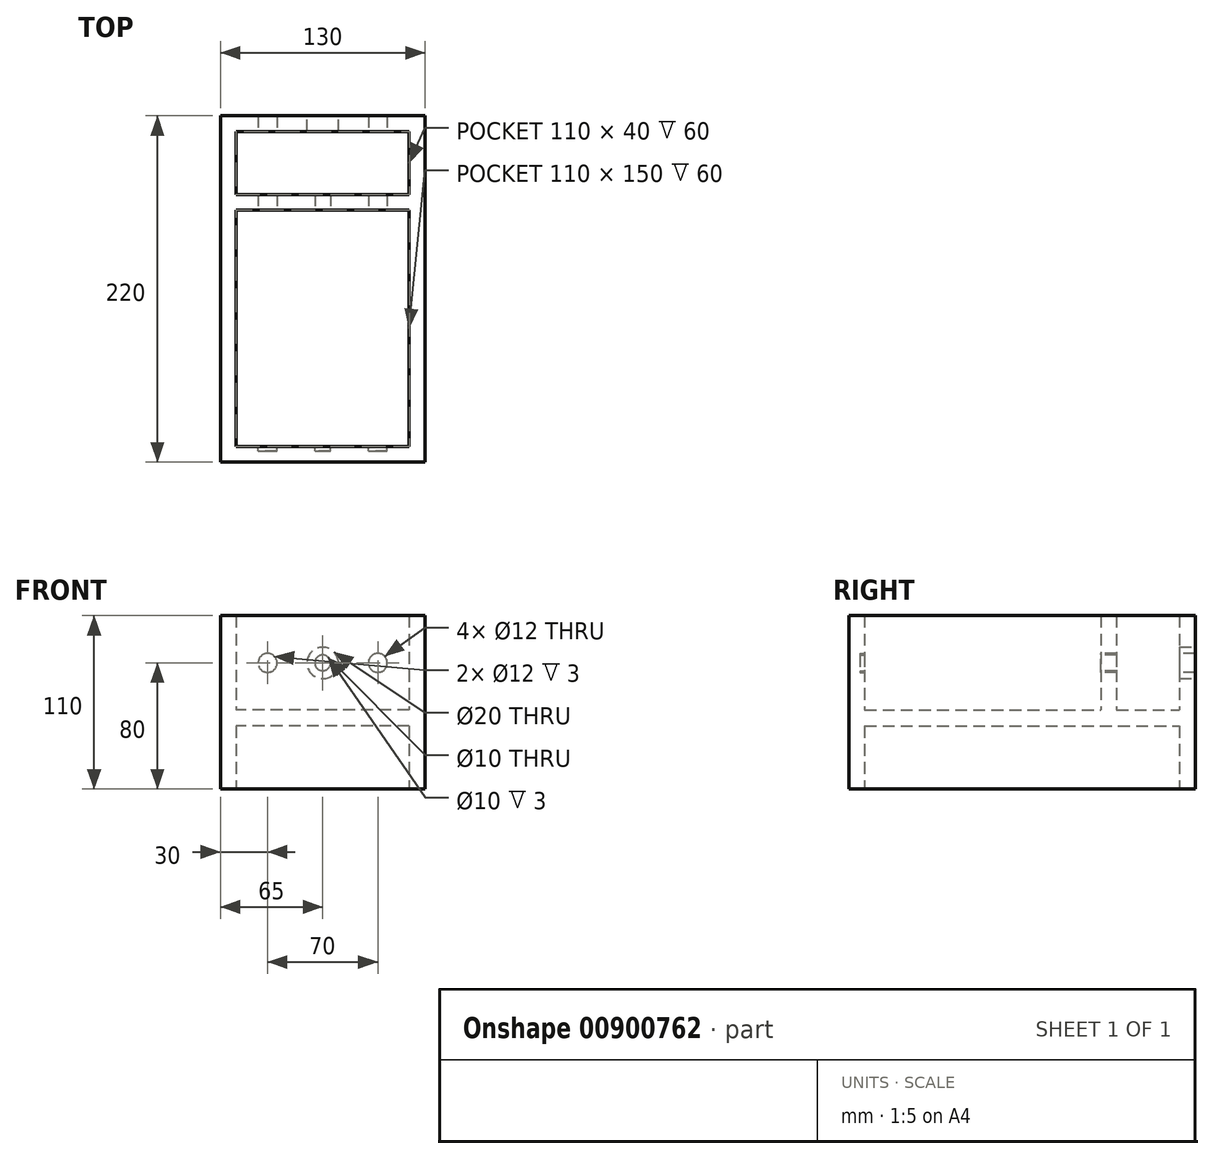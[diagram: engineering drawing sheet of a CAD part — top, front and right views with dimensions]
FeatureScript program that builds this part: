
annotation { "Feature Type Name" : "Feature", "Feature Type Description" : "" }
export const myFeature = defineFeature(function(context is Context, id is Id, definition is map)
    precondition{}
    {
        {
            var Q0;
            Q0=qCreatedBy(makeId("Right.planeOp"),FACE);
            var sketch = newSketch(context, id + "F0", { "sketchPlane" : qUnion([Q0])});
            skLineSegment(sketch, "E0.bottom", {"start": v(-110, 70) * mm, "end": v(-100, 70) * mm});
            skLineSegment(sketch, "E0.top", {"start": v(-110, -40) * mm, "end": v(-100, -40) * mm});
            skLineSegment(sketch, "E0.left", {"start": v(-110, 70) * mm, "end": v(-110, -40) * mm});
            skLineSegment(sketch, "E0.right", {"start": v(-100, 70) * mm, "end": v(-100, -40) * mm});
            skLineSegment(sketch, "E1.bottom", {"start": v(-100, 0) * mm, "end": v(100, 0) * mm});
            skLineSegment(sketch, "E1.top", {"start": v(-100, 10) * mm, "end": v(100, 10) * mm});
            skLineSegment(sketch, "E1.left", {"start": v(-100, 10) * mm, "end": v(-100, 0) * mm});
            skLineSegment(sketch, "E1.right", {"start": v(100, 10) * mm, "end": v(100, 0) * mm});
            skLineSegment(sketch, "E2.bottom", {"start": v(50, 70) * mm, "end": v(60, 70) * mm});
            skLineSegment(sketch, "E2.top", {"start": v(50, 10) * mm, "end": v(60, 10) * mm});
            skLineSegment(sketch, "E2.left", {"start": v(50, 70) * mm, "end": v(50, 10) * mm});
            skLineSegment(sketch, "E2.right", {"start": v(60, 70) * mm, "end": v(60, 10) * mm});
            skLineSegment(sketch, "E3.bottom", {"start": v(110, 70) * mm, "end": v(100, 70) * mm});
            skLineSegment(sketch, "E3.top", {"start": v(110, -40) * mm, "end": v(100, -40) * mm});
            skLineSegment(sketch, "E3.left", {"start": v(110, 70) * mm, "end": v(110, -40) * mm});
            skLineSegment(sketch, "E3.right", {"start": v(100, 70) * mm, "end": v(100, -40) * mm});
            skSolve(sketch);
        }
        {
            var Q0;
            {var subQ2=sQuery(id+"F0.wireOp",EDGE,"E3.bottom");Q0=makeQuery(id+"F0.imprint","IMPRINT",FACE,{"disambiguationData":[TD([[makeQuery(id+"F0.imprint","IMPRINT",EDGE,{"derivedFrom":subQ2}),1.0]])]});}
            var Q1;
            {var subQ5=sQuery(id+"F0.wireOp",EDGE,"E1.bottom");Q1=makeQuery(id+"F0.imprint","IMPRINT",FACE,{"disambiguationData":[TD([[makeQuery(id+"F0.imprint","IMPRINT",EDGE,{"derivedFrom":subQ5}),1.0]])]});}
            var Q2;
            Q2=makeQuery(id+"F0.imprint","IMPRINT",FACE,{"disambiguationData":[TD([[makeQuery(id+"F0.imprint","IMPRINT",EDGE,{"derivedFrom":sQuery(id+"F0.wireOp",EDGE,"E2.bottom")}),-1.0]])]});
            var Q3;
            {var subQ1=sQuery(id+"F0.wireOp",EDGE,"E0.bottom");Q3=makeQuery(id+"F0.imprint","IMPRINT",FACE,{"disambiguationData":[TD([[makeQuery(id+"F0.imprint","IMPRINT",EDGE,{"derivedFrom":subQ1}),-1.0]])]});}
            extrude(context, id + "F1", {"entities" : qUnion([Q0, Q1, Q2, Q3]), "endBound" : BoundingType.SYMMETRIC, "depth" : 110 * mm, "offsetDistance" : 25 * mm});
        }
        {
            var Q0;
            Q0=makeQuery(id+"F1.opExtrude","CAP_FACE",FACE,{"disambiguationData":[OSD([sQuery(id+"F0.wireOp",EDGE,"E0.bottom"),sQuery(id+"F0.wireOp",EDGE,"E0.top"),sQuery(id+"F0.wireOp",EDGE,"E0.left"),sQuery(id+"F0.wireOp",EDGE,"E0.right"),sQuery(id+"F0.wireOp",EDGE,"E1.bottom"),sQuery(id+"F0.wireOp",EDGE,"E1.top"),sQuery(id+"F0.wireOp",EDGE,"E2.bottom"),sQuery(id+"F0.wireOp",EDGE,"E2.left"),sQuery(id+"F0.wireOp",EDGE,"E2.right"),sQuery(id+"F0.wireOp",EDGE,"E3.bottom"),sQuery(id+"F0.wireOp",EDGE,"E3.top"),sQuery(id+"F0.wireOp",EDGE,"E3.left"),sQuery(id+"F0.wireOp",EDGE,"E3.right")])],"isStart":false});
            var sketch = newSketch(context, id + "F2", { "sketchPlane" : qUnion([Q0])});
            skLineSegment(sketch, "E4.bottom", {"start": v(-110, 70) * mm, "end": v(110, 70) * mm});
            skLineSegment(sketch, "E4.top", {"start": v(-110, -40) * mm, "end": v(110, -40) * mm});
            skLineSegment(sketch, "E4.left", {"start": v(-110, 70) * mm, "end": v(-110, -40) * mm});
            skLineSegment(sketch, "E4.right", {"start": v(110, 70) * mm, "end": v(110, -40) * mm});
            skSolve(sketch);
        }
        {
            var Q0;
            Q0 = qSketchRegion(id + "F2", true);
            extrude(context, id + "F3", {"entities" : qUnion([Q0]), "operationType" : NewBodyOperationType.ADD, "depth" : 10 * mm, "offsetDistance" : 25 * mm});
        }
        {
            var Q0;
            Q0=makeQuery(id+"F1.opExtrude","SWEPT_BODY",BODY,{"disambiguationData":[OSD([sQuery(id+"F0.wireOp",EDGE,"E0.bottom"),sQuery(id+"F0.wireOp",EDGE,"E0.top"),sQuery(id+"F0.wireOp",EDGE,"E0.left"),sQuery(id+"F0.wireOp",EDGE,"E0.right"),sQuery(id+"F0.wireOp",EDGE,"E1.bottom"),sQuery(id+"F0.wireOp",EDGE,"E1.top"),sQuery(id+"F0.wireOp",EDGE,"E2.bottom"),sQuery(id+"F0.wireOp",EDGE,"E2.left"),sQuery(id+"F0.wireOp",EDGE,"E2.right"),sQuery(id+"F0.wireOp",EDGE,"E3.bottom"),sQuery(id+"F0.wireOp",EDGE,"E3.top"),sQuery(id+"F0.wireOp",EDGE,"E3.left"),sQuery(id+"F0.wireOp",EDGE,"E3.right")])]});
            var Q1;
            Q1=qCreatedBy(makeId("Right.planeOp"),FACE);
            mirror(context, id + "F4", {"operationType" : NewBodyOperationType.ADD, "entities" : qUnion([Q0]), "mirrorPlane" : qUnion([Q1])});
        }
        {
            var Q0;
            Q0=makeQuery(id+"F1.opExtrude","SWEPT_FACE",FACE,{"disambiguationData":[OSD([sQuery(id+"F0.wireOp",EDGE,"E3.left")])]});
            var sketch = newSketch(context, id + "F5", { "sketchPlane" : qUnion([Q0])});
            skCircle(sketch, "E5", {"center": v(0, 40) * mm, "radius": 10 * mm});
            skSolve(sketch);
        }
        {
            var Q0;
            Q0 = qSketchRegion(id + "F5", true);
            extrude(context, id + "F6", {"entities" : qUnion([Q0]), "operationType" : NewBodyOperationType.REMOVE, "endBound" : BoundingType.UP_TO_NEXT, "oppositeDirection" : true, "depth" : 25 * mm, "offsetDistance" : 25 * mm});
        }
        {
            var Q0;
            Q0=makeQuery(id+"F1.opExtrude","SWEPT_FACE",FACE,{"disambiguationData":[OSD([sQuery(id+"F0.wireOp",EDGE,"E2.left")])]});
            var sketch = newSketch(context, id + "F7", { "sketchPlane" : qUnion([Q0])});
            skCircle(sketch, "E6", {"center": v(0, 40) * mm, "radius": 5 * mm});
            skSolve(sketch);
        }
        {
            var Q0;
            Q0 = qSketchRegion(id + "F7", true);
            extrude(context, id + "F8", {"entities" : qUnion([Q0]), "operationType" : NewBodyOperationType.REMOVE, "endBound" : BoundingType.UP_TO_NEXT, "oppositeDirection" : true, "depth" : 25 * mm, "offsetDistance" : 25 * mm});
        }
        {
            var Q0;
            {var subQ0=sQuery(id+"F0.wireOp",EDGE,"E0.right");Q0=makeQuery(id+"F1.opExtrude","SWEPT_FACE",FACE,{"disambiguationData":[OSD([subQ0]),TDD([makeQuery(id+"F0.imprint","IMPRINT",EDGE,{"disambiguationData":[TD([[makeQuery(id+"F0.imprint","INTERSECT",VERTEX,{"derivedFrom":[sQuery(id+"F0.wireOp",EDGE,"E0.bottom"),subQ0]}),-1.0]])],"derivedFrom":subQ0})])]});}
            var sketch = newSketch(context, id + "F9", { "sketchPlane" : qUnion([Q0])});
            skCircle(sketch, "E7", {"center": v(0, 40) * mm, "radius": 5 * mm});
            skLineSegment(sketch, "E8", {"start": v(35, 40) * mm, "end": v(-35, 40) * mm, "construction": true});
            skCircle(sketch, "E9", {"center": v(35, 40) * mm, "radius": 6 * mm});
            skCircle(sketch, "E10", {"center": v(-35, 40) * mm, "radius": 6 * mm});
            skSolve(sketch);
        }
        {
            var Q0;
            Q0 = qSketchRegion(id + "F9", true);
            extrude(context, id + "F10", {"entities" : qUnion([Q0]), "operationType" : NewBodyOperationType.REMOVE, "oppositeDirection" : true, "depth" : 3 * mm, "offsetDistance" : 25 * mm});
        }
        {
            var Q0;
            Q0=makeQuery(id+"F1.opExtrude","SWEPT_FACE",FACE,{"disambiguationData":[OSD([sQuery(id+"F0.wireOp",EDGE,"E2.left")])]});
            var sketch = newSketch(context, id + "F11", { "sketchPlane" : qUnion([Q0])});
            skCircle(sketch, "E11", {"center": v(-35, 40) * mm, "radius": 6 * mm});
            skCircle(sketch, "E12", {"center": v(35, 40) * mm, "radius": 6 * mm});
            skSolve(sketch);
        }
        {
            var Q0;
            Q0=makeQuery(id+"F11.imprint","IMPRINT",FACE,{"disambiguationData":[TD([[makeQuery(id+"F11.imprint","IMPRINT",EDGE,{"derivedFrom":sQuery(id+"F11.wireOp",EDGE,"E11")}),1.0]])]});
            var Q1;
            Q1=makeQuery(id+"F11.imprint","IMPRINT",FACE,{"disambiguationData":[TD([[makeQuery(id+"F11.imprint","IMPRINT",EDGE,{"derivedFrom":sQuery(id+"F11.wireOp",EDGE,"E12")}),1.0]])]});
            extrude(context, id + "F12", {"entities" : qUnion([Q0, Q1]), "operationType" : NewBodyOperationType.REMOVE, "endBound" : BoundingType.THROUGH_ALL, "oppositeDirection" : true, "depth" : 25 * mm, "offsetDistance" : 25 * mm});
        }
    });
